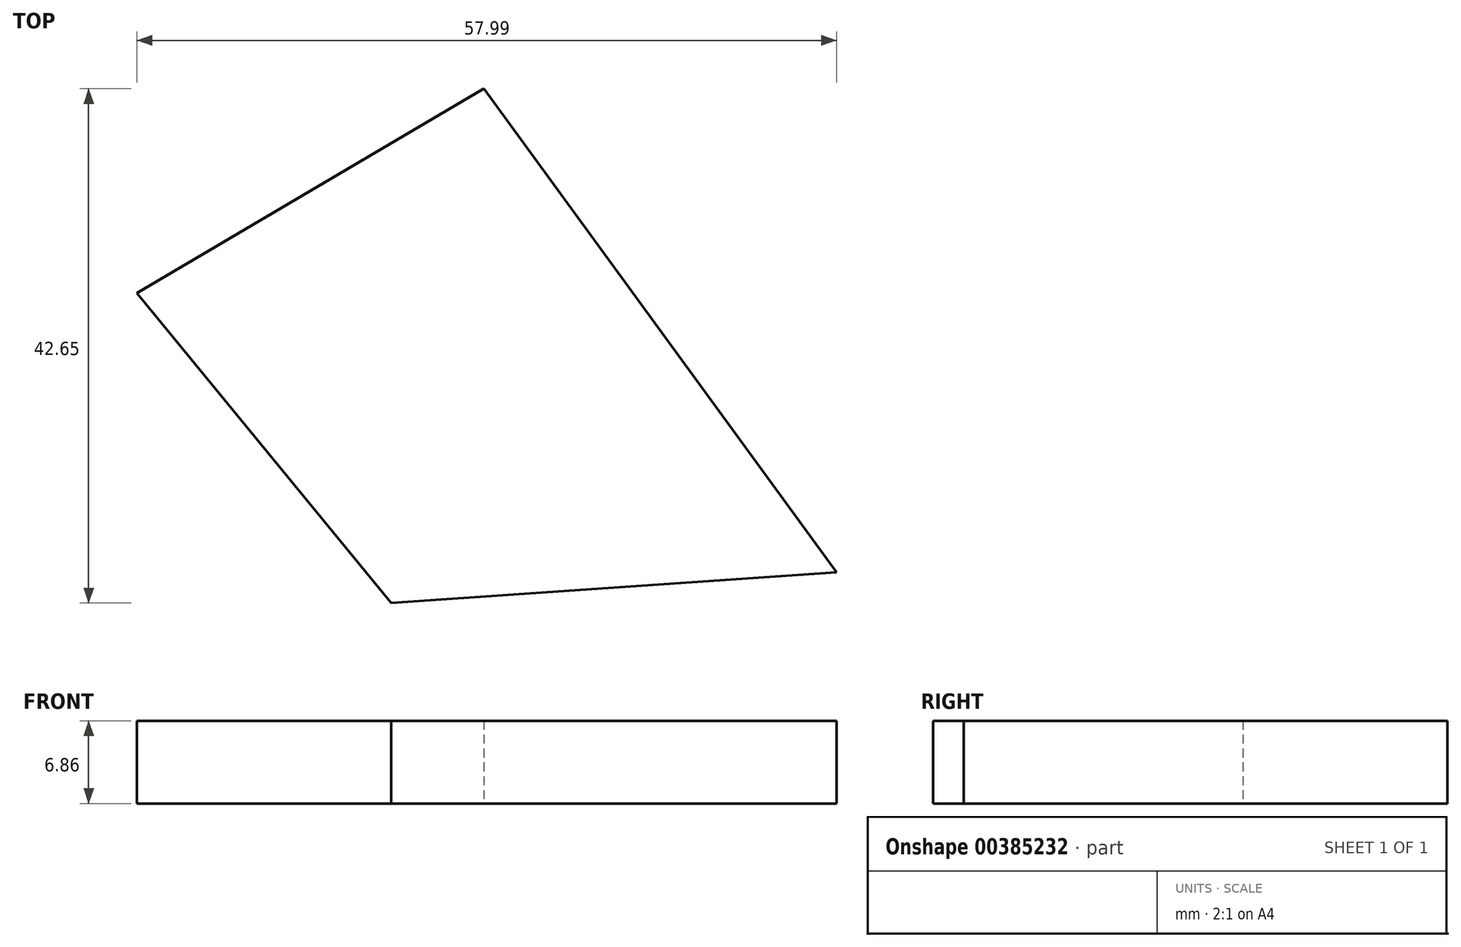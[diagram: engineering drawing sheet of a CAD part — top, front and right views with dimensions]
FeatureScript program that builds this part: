
annotation { "Feature Type Name" : "Feature", "Feature Type Description" : "" }
export const myFeature = defineFeature(function(context is Context, id is Id, definition is map)
    precondition{}
    {
        {
            var Q0;
            Q0=qCreatedBy(makeId("Top.planeOp"),FACE);
            var sketch = newSketch(context, id + "F0", { "sketchPlane" : qUnion([Q0])});
            skLineSegment(sketch, "E0", {"start": v(-30.52, 16.35) * mm, "end": v(-9.44, -9.34) * mm});
            skLineSegment(sketch, "E1", {"start": v(-9.44, -9.34) * mm, "end": v(27.47, -6.79) * mm});
            skLineSegment(sketch, "E2", {"start": v(27.47, -6.79) * mm, "end": v(-1.76, 33.3) * mm});
            skLineSegment(sketch, "E3", {"start": v(-1.76, 33.3) * mm, "end": v(-30.52, 16.35) * mm});
            skSolve(sketch);
        }
        {
            var Q0;
            Q0 = qSketchRegion(id + "F0", true);
            extrude(context, id + "F1", {"entities" : qUnion([Q0]), "depth" : 6.86 * mm});
        }
    });
